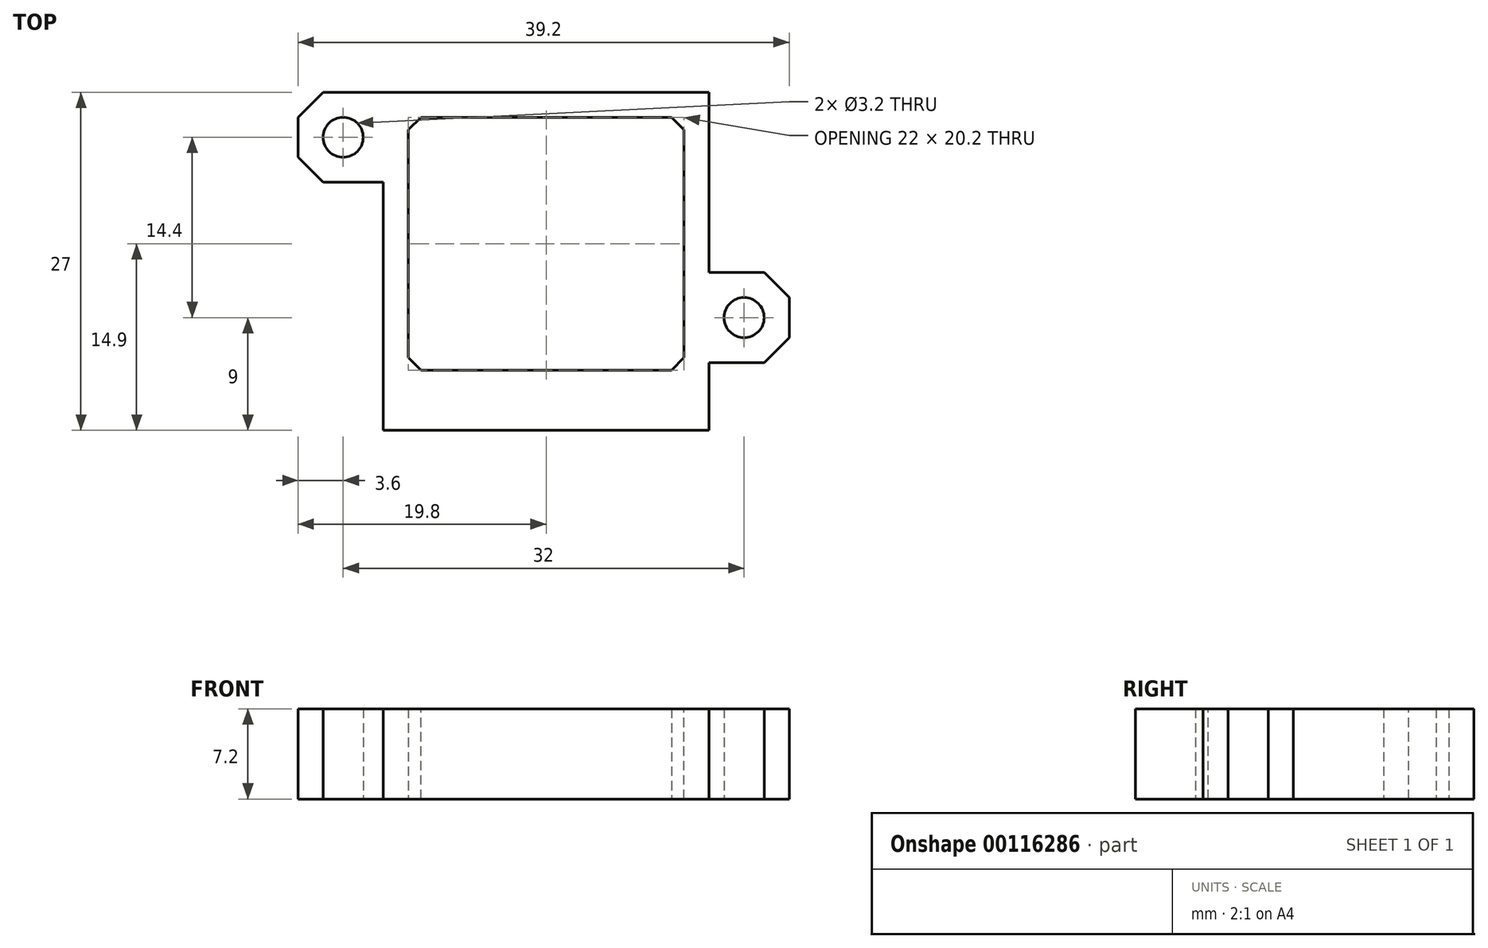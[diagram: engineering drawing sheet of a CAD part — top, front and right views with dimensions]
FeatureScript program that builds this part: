
annotation { "Feature Type Name" : "Feature", "Feature Type Description" : "" }
export const myFeature = defineFeature(function(context is Context, id is Id, definition is map)
    precondition{}
    {
        {
            var Q0;
            Q0=qCreatedBy(makeId("Top.planeOp"),FACE);
            var sketch = newSketch(context, id + "F0", { "sketchPlane" : qUnion([Q0])});
            skLineSegment(sketch, "E0.bottom", {"start": v(11, -10.1) * mm, "end": v(-11, -10.1) * mm});
            skLineSegment(sketch, "E0.top", {"start": v(11, 10.1) * mm, "end": v(-11, 10.1) * mm});
            skLineSegment(sketch, "E0.left", {"start": v(11, -10.1) * mm, "end": v(11, 10.1) * mm});
            skLineSegment(sketch, "E0.right", {"start": v(-11, -10.1) * mm, "end": v(-11, 10.1) * mm});
            skPoint(sketch, "E0.middle", {"position": v(0, 0) * mm});
            skLineSegment(sketch, "E1", {"start": v(-19.8, 12.1) * mm, "end": v(13, 12.1) * mm});
            skLineSegment(sketch, "E2", {"start": v(13, 12.1) * mm, "end": v(13, -2.3) * mm});
            skLineSegment(sketch, "E3", {"start": v(13, -2.3) * mm, "end": v(19.4, -2.3) * mm});
            skLineSegment(sketch, "E4", {"start": v(19.4, -2.3) * mm, "end": v(19.4, -9.5) * mm});
            skLineSegment(sketch, "E5", {"start": v(19.4, -9.5) * mm, "end": v(13, -9.5) * mm});
            skLineSegment(sketch, "E6", {"start": v(13, -9.5) * mm, "end": v(13, -10.1) * mm});
            skLineSegment(sketch, "E7", {"start": v(13, -10.1) * mm, "end": v(13, -14.9) * mm});
            skLineSegment(sketch, "E8", {"start": v(13, -14.9) * mm, "end": v(-13, -14.9) * mm});
            skLineSegment(sketch, "E9", {"start": v(-13, -14.9) * mm, "end": v(-13, 4.9) * mm});
            skLineSegment(sketch, "E10", {"start": v(-13, 4.9) * mm, "end": v(-19.8, 4.9) * mm});
            skLineSegment(sketch, "E11", {"start": v(-19.8, 4.9) * mm, "end": v(-19.8, 12.1) * mm});
            skPoint(sketch, "E12", {"position": v(-16.2, 8.5) * mm});
            skPoint(sketch, "E13", {"position": v(15.8, -5.9) * mm});
            skCircle(sketch, "E14", {"center": v(15.8, -5.9) * mm, "radius": 1.6 * mm});
            skCircle(sketch, "E15", {"center": v(-16.2, 8.5) * mm, "radius": 1.6 * mm});
            skSolve(sketch);
        }
        {
            var Q0;
            Q0=makeQuery(id+"F0.imprint","IMPRINT",FACE,{"disambiguationData":[TD([[makeQuery(id+"F0.imprint","IMPRINT",EDGE,{"derivedFrom":sQuery(id+"F0.wireOp",EDGE,"E0.bottom")}),1.0]])]});
            extrude(context, id + "F1", {"entities" : qUnion([Q0]), "depth" : 7.2 * mm});
        }
        {
            var Q0;
            Q0=makeQuery(id+"F1.opExtrude","SWEPT_EDGE",EDGE,{"disambiguationData":[OSD([sQuery(id+"F0.wireOp",EDGE,"E10"),sQuery(id+"F0.wireOp",EDGE,"E11")])]});
            var Q1;
            Q1=makeQuery(id+"F1.opExtrude","SWEPT_EDGE",EDGE,{"disambiguationData":[OSD([sQuery(id+"F0.wireOp",EDGE,"E1"),sQuery(id+"F0.wireOp",EDGE,"E11")])]});
            var Q2;
            Q2=makeQuery(id+"F1.opExtrude","SWEPT_EDGE",EDGE,{"disambiguationData":[OSD([sQuery(id+"F0.wireOp",EDGE,"E4"),sQuery(id+"F0.wireOp",EDGE,"E5")])]});
            var Q3;
            Q3=makeQuery(id+"F1.opExtrude","SWEPT_EDGE",EDGE,{"disambiguationData":[OSD([sQuery(id+"F0.wireOp",EDGE,"E3"),sQuery(id+"F0.wireOp",EDGE,"E4")])]});
            chamfer(context, id + "F2", {"entities" : qUnion([Q0, Q1, Q2, Q3]), "width" : 2 * mm, "tangentPropagation" : true});
        }
        {
            var Q0;
            Q0=makeQuery(id+"F1.opExtrude","SWEPT_EDGE",EDGE,{"disambiguationData":[OSD([sQuery(id+"F0.wireOp",EDGE,"E0.top"),sQuery(id+"F0.wireOp",EDGE,"E0.left")])]});
            var Q1;
            Q1=makeQuery(id+"F1.opExtrude","SWEPT_EDGE",EDGE,{"disambiguationData":[OSD([sQuery(id+"F0.wireOp",EDGE,"E0.top"),sQuery(id+"F0.wireOp",EDGE,"E0.right")])]});
            var Q2;
            Q2=makeQuery(id+"F1.opExtrude","SWEPT_EDGE",EDGE,{"disambiguationData":[OSD([sQuery(id+"F0.wireOp",EDGE,"E0.bottom"),sQuery(id+"F0.wireOp",EDGE,"E0.right")])]});
            var Q3;
            Q3=makeQuery(id+"F1.opExtrude","SWEPT_EDGE",EDGE,{"disambiguationData":[OSD([sQuery(id+"F0.wireOp",EDGE,"E0.bottom"),sQuery(id+"F0.wireOp",EDGE,"E0.left")])]});
            chamfer(context, id + "F3", {"entities" : qUnion([Q0, Q1, Q2, Q3]), "width" : 1 * mm, "tangentPropagation" : true});
        }
    });
